# Revit family: Primo 3-674-xx e
name_source: partatom
category: Lighting Fixtures
units: mm (PartAtom-declared; Revit-internal decimal feet)

## family parameters
Always vertical = Yes
Cut with Voids When Loaded = No
Host = Ceiling
Light Source = Yes
OmniClass Number = 23.80.70.11
OmniClass Title = Luminaries for Internal Lighting
Part Type = Normal
Room Calculation Point = No
Round Connector Dimension = Use Diameter
Shared = No

## types (4) — shared parameters
Color Filter = 16777215
Dimming Lamp Color Temperature Shift = <None>
Lamp = LED Array
Main Diffuser = Clear Glass
Manufacturer = Oxygen - Lighting & Fans
Model = 3-674-xx / Primo Pendants
Photometric Web File = 3-674-40 Primo Pendant.ies
References = Ref. 3 = 120 V / Ref. 37 = 277 V
Tilt Angle = 90.00°
URL = www.oxygenlighting.com
Voltage Input = 120 V or 277 V - 50/60 Hz
Wattage Comments = 7 x 18.77 W at 120 V
zero-valued in all types: Default Elevation

## per-type parameters (varying)
| type | Metal Finish | Voltage |
| 3-674-40 / Aged Brass | 40 - Aged Brass | 120 V |
| 3-674-24 / Satin Nickel | 24 - Satin Nickel | 120 V |
| 37-674-24 / Satin Nickel | 24 - Satin Nickel | 277 V |
| 37-674-40 / Aged Brass | 40 - Aged Brass | 277 V |

## geometry (parser evidence)
native form markers: Sweep x11
no freeform markers — native parametric forms only
